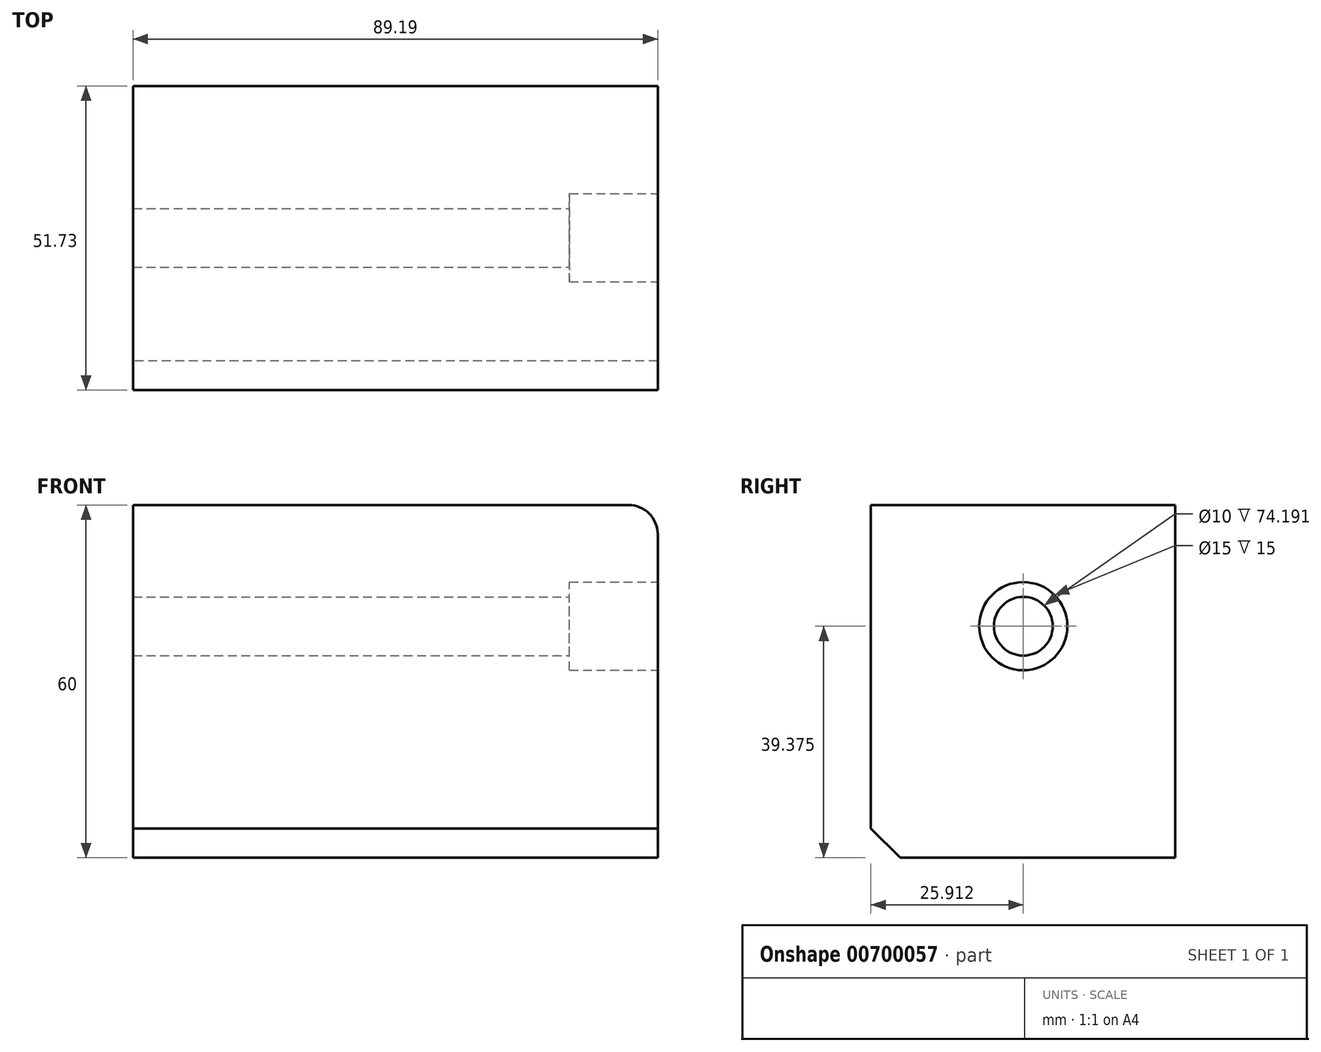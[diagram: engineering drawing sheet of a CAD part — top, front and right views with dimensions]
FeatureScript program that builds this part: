
annotation { "Feature Type Name" : "Feature", "Feature Type Description" : "" }
export const myFeature = defineFeature(function(context is Context, id is Id, definition is map)
    precondition{}
    {
        {
            var Q0;
            Q0=qCreatedBy(makeId("Top.planeOp"),FACE);
            var sketch = newSketch(context, id + "F0", { "sketchPlane" : qUnion([Q0])});
            skLineSegment(sketch, "E0.bottom", {"start": v(0, 51.73) * mm, "end": v(89.2, 51.73) * mm});
            skLineSegment(sketch, "E0.top", {"start": v(0, 0) * mm, "end": v(89.2, 0) * mm});
            skLineSegment(sketch, "E0.left", {"start": v(0, 51.73) * mm, "end": v(0, 0) * mm});
            skLineSegment(sketch, "E0.right", {"start": v(89.2, 51.73) * mm, "end": v(89.2, 0) * mm});
            skSolve(sketch);
        }
        {
            var Q0;
            Q0=makeQuery(id+"F0.imprint","IMPRINT",FACE,{"disambiguationData":[TD([[makeQuery(id+"F0.imprint","IMPRINT",EDGE,{"derivedFrom":sQuery(id+"F0.wireOp",EDGE,"E0.bottom")}),-1.0]])]});
            extrude(context, id + "F1", {"entities" : qUnion([Q0]), "depth" : 60 * mm, "offsetDistance" : 25 * mm});
        }
        {
            var Q0;
            Q0=makeQuery(id+"F1.opExtrude","CAP_EDGE",EDGE,{"disambiguationData":[OSD([sQuery(id+"F0.wireOp",EDGE,"E0.right")])],"isStart":false});
            fillet(context, id + "F2", {"entities" : qUnion([Q0]), "radius" : 5 * mm, "tangentPropagation" : true, "allowEdgeOverflow" : false});
        }
        {
            var Q0;
            Q0=makeQuery(id+"F1.opExtrude","CAP_EDGE",EDGE,{"disambiguationData":[OSD([sQuery(id+"F0.wireOp",EDGE,"E0.top")])],"isStart":true});
            chamfer(context, id + "F3", {"entities" : qUnion([Q0]), "width" : 5 * mm, "tangentPropagation" : true});
        }
        {
            var Q0;
            Q0=makeQuery(id+"F1.opExtrude","SWEPT_FACE",FACE,{"disambiguationData":[OSD([sQuery(id+"F0.wireOp",EDGE,"E0.right")])]});
            var sketch = newSketch(context, id + "F4", { "sketchPlane" : qUnion([Q0])});
            skCircle(sketch, "E1", {"center": v(25.91, 39.38) * mm, "radius": 5.24 * mm});
            skSolve(sketch);
        }
        {
            var Q0;
            Q0=sQuery(id+"F4.wireOp",VERTEX,"E1.center");
            var Q1;
            Q1=makeQuery(id+"F1.opExtrude","SWEPT_BODY",BODY,{"disambiguationData":[OSD([sQuery(id+"F0.wireOp",EDGE,"E0.bottom"),sQuery(id+"F0.wireOp",EDGE,"E0.top"),sQuery(id+"F0.wireOp",EDGE,"E0.left"),sQuery(id+"F0.wireOp",EDGE,"E0.right")])]});
            hole(context, id + "F5", {"style" : HoleStyle.C_BORE, "endStyle" : HoleEndStyle.THROUGH, "holeDiameter" : 10 * mm, "cBoreDiameter" : 15 * mm, "cBoreDepth" : 15 * mm, "majorDiameter" : 5 * mm, "isTappedThrough" : true, "tappedDepth" : 12 * mm, "tapClearance" : 3, "locations" : qUnion([Q0]), "scope" : qUnion([Q1])});
        }
    });
